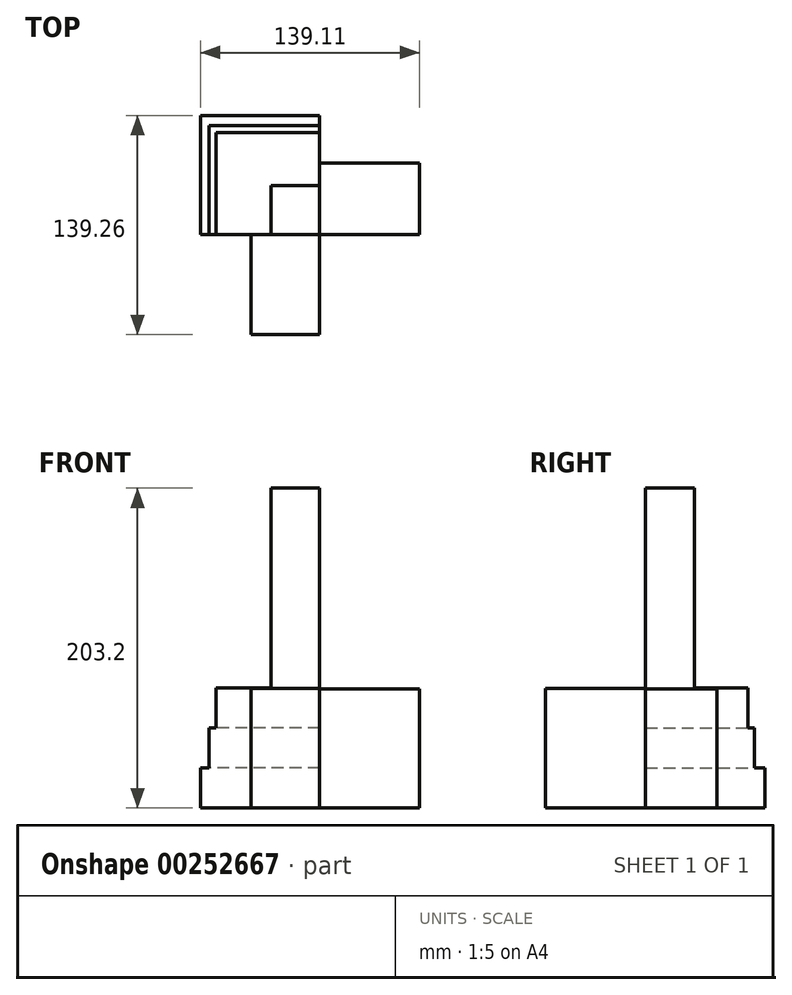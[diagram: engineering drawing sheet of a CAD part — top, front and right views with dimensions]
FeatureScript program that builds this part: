
annotation { "Feature Type Name" : "Feature", "Feature Type Description" : "" }
export const myFeature = defineFeature(function(context is Context, id is Id, definition is map)
    precondition{}
    {
        {
            var Q0;
            Q0=qCreatedBy(makeId("Top.planeOp"),FACE);
            var sketch = newSketch(context, id + "F0", { "sketchPlane" : qUnion([Q0])});
            skLineSegment(sketch, "E0.bottom", {"start": v(0, 0) * mm, "end": v(-75.6, 0) * mm});
            skLineSegment(sketch, "E0.top", {"start": v(0, 75.76) * mm, "end": v(-75.6, 75.76) * mm});
            skLineSegment(sketch, "E0.left", {"start": v(0, 0) * mm, "end": v(0, 75.76) * mm});
            skLineSegment(sketch, "E0.right", {"start": v(-75.6, 0) * mm, "end": v(-75.6, 75.76) * mm});
            skSolve(sketch);
        }
        {
            var Q0;
            Q0=makeQuery(id+"F0.imprint","IMPRINT",FACE,{"disambiguationData":[TD([[makeQuery(id+"F0.imprint","IMPRINT",EDGE,{"derivedFrom":sQuery(id+"F0.wireOp",EDGE,"E0.bottom")}),-1.0]])]});
            extrude(context, id + "F1", {"entities" : qUnion([Q0]), "depth" : 25.4 * mm});
        }
        {
            var Q0;
            Q0=makeQuery(id+"F1.opExtrude","CAP_FACE",FACE,{"disambiguationData":[OSD([sQuery(id+"F0.wireOp",EDGE,"E0.bottom"),sQuery(id+"F0.wireOp",EDGE,"E0.top"),sQuery(id+"F0.wireOp",EDGE,"E0.left"),sQuery(id+"F0.wireOp",EDGE,"E0.right")])],"isStart":false});
            var sketch = newSketch(context, id + "F2", { "sketchPlane" : qUnion([Q0])});
            skLineSegment(sketch, "E1.bottom", {"start": v(0, 0) * mm, "end": v(-70.14, 0) * mm});
            skLineSegment(sketch, "E1.top", {"start": v(0, 69.2) * mm, "end": v(-70.14, 69.2) * mm});
            skLineSegment(sketch, "E1.left", {"start": v(0, 0) * mm, "end": v(0, 69.2) * mm});
            skLineSegment(sketch, "E1.right", {"start": v(-70.14, 0) * mm, "end": v(-70.14, 69.2) * mm});
            skSolve(sketch);
        }
        {
            var Q0;
            Q0 = qSketchRegion(id + "F2", true);
            extrude(context, id + "F3", {"entities" : qUnion([Q0]), "operationType" : NewBodyOperationType.ADD, "depth" : 25.4 * mm});
        }
        {
            var Q0;
            Q0=makeQuery(id+"F3.opExtrude","CAP_FACE",FACE,{"disambiguationData":[OSD([sQuery(id+"F2.wireOp",EDGE,"E1.bottom"),sQuery(id+"F2.wireOp",EDGE,"E1.top"),sQuery(id+"F2.wireOp",EDGE,"E1.left"),sQuery(id+"F2.wireOp",EDGE,"E1.right")])],"isStart":false});
            var sketch = newSketch(context, id + "F4", { "sketchPlane" : qUnion([Q0])});
            skLineSegment(sketch, "E2.bottom", {"start": v(0, 0) * mm, "end": v(-65.87, 0) * mm});
            skLineSegment(sketch, "E2.top", {"start": v(0, 64.92) * mm, "end": v(-65.87, 64.92) * mm});
            skLineSegment(sketch, "E2.left", {"start": v(0, 0) * mm, "end": v(0, 64.92) * mm});
            skLineSegment(sketch, "E2.right", {"start": v(-65.87, 0) * mm, "end": v(-65.87, 64.92) * mm});
            skSolve(sketch);
        }
        {
            var Q0;
            Q0 = qSketchRegion(id + "F4", true);
            extrude(context, id + "F5", {"entities" : qUnion([Q0]), "operationType" : NewBodyOperationType.ADD, "depth" : 25.4 * mm});
        }
        {
            var Q0;
            Q0=makeQuery(id+"F5.opExtrude","CAP_FACE",FACE,{"disambiguationData":[OSD([sQuery(id+"F4.wireOp",EDGE,"E2.bottom"),sQuery(id+"F4.wireOp",EDGE,"E2.top"),sQuery(id+"F4.wireOp",EDGE,"E2.left"),sQuery(id+"F4.wireOp",EDGE,"E2.right")])],"isStart":false});
            var sketch = newSketch(context, id + "F6", { "sketchPlane" : qUnion([Q0])});
            skLineSegment(sketch, "E3.bottom", {"start": v(0, 0) * mm, "end": v(-30.8, 0) * mm});
            skLineSegment(sketch, "E3.top", {"start": v(0, 31.07) * mm, "end": v(-30.8, 31.07) * mm});
            skLineSegment(sketch, "E3.left", {"start": v(0, 0) * mm, "end": v(0, 31.07) * mm});
            skLineSegment(sketch, "E3.right", {"start": v(-30.8, 0) * mm, "end": v(-30.8, 31.07) * mm});
            skSolve(sketch);
        }
        {
            var Q0;
            Q0=makeQuery(id+"F6.imprint","IMPRINT",FACE,{"disambiguationData":[TD([[makeQuery(id+"F6.imprint","IMPRINT",EDGE,{"derivedFrom":sQuery(id+"F6.wireOp",EDGE,"E3.bottom")}),-1.0]])]});
            extrude(context, id + "F7", {"entities" : qUnion([Q0]), "operationType" : NewBodyOperationType.ADD, "depth" : 127 * mm});
        }
        {
            var Q0;
            Q0=qCreatedBy(makeId("Front.planeOp"),FACE);
            var sketch = newSketch(context, id + "F8", { "sketchPlane" : qUnion([Q0])});
            skLineSegment(sketch, "E4.bottom", {"start": v(0, 0) * mm, "end": v(-43.68, 0) * mm});
            skLineSegment(sketch, "E4.top", {"start": v(0, 75.94) * mm, "end": v(-43.68, 75.94) * mm});
            skLineSegment(sketch, "E4.left", {"start": v(0, 0) * mm, "end": v(0, 75.94) * mm});
            skLineSegment(sketch, "E4.right", {"start": v(-43.68, 0) * mm, "end": v(-43.68, 75.94) * mm});
            skSolve(sketch);
        }
        {
            var Q0;
            Q0 = qSketchRegion(id + "F8", true);
            extrude(context, id + "F9", {"entities" : qUnion([Q0]), "operationType" : NewBodyOperationType.ADD, "depth" : 63.5 * mm});
        }
        {
            var Q0;
            Q0=qCreatedBy(makeId("Right.planeOp"),FACE);
            var sketch = newSketch(context, id + "F10", { "sketchPlane" : qUnion([Q0])});
            skLineSegment(sketch, "E5.bottom", {"start": v(0, 0) * mm, "end": v(45.35, 0) * mm});
            skLineSegment(sketch, "E5.top", {"start": v(0, 75.62) * mm, "end": v(45.35, 75.62) * mm});
            skLineSegment(sketch, "E5.left", {"start": v(0, 0) * mm, "end": v(0, 75.62) * mm});
            skLineSegment(sketch, "E5.right", {"start": v(45.35, 0) * mm, "end": v(45.35, 75.62) * mm});
            skSolve(sketch);
        }
        {
            var Q0;
            Q0 = qSketchRegion(id + "F10", true);
            extrude(context, id + "F11", {"entities" : qUnion([Q0]), "operationType" : NewBodyOperationType.ADD, "depth" : 63.5 * mm});
        }
    });
